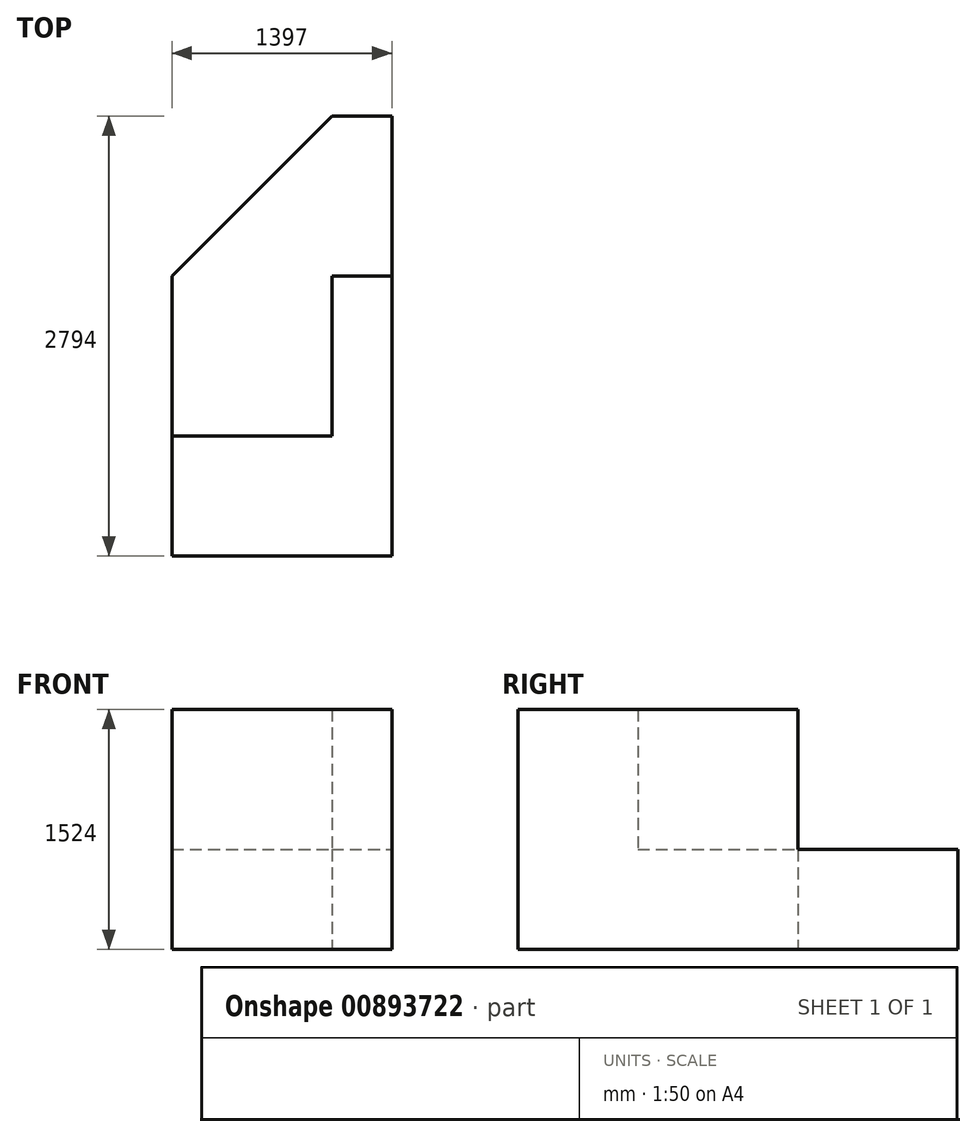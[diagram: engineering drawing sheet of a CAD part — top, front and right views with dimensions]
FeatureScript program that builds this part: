
annotation { "Feature Type Name" : "Feature", "Feature Type Description" : "" }
export const myFeature = defineFeature(function(context is Context, id is Id, definition is map)
    precondition{}
    {
        {
            var Q0;
            Q0=qCreatedBy(makeId("Top.planeOp"),FACE);
            var sketch = newSketch(context, id + "F0", { "sketchPlane" : qUnion([Q0])});
            skLineSegment(sketch, "E0", {"start": v(0, 0) * mm, "end": v(1397, 0) * mm});
            skLineSegment(sketch, "E1", {"start": v(1397, 0) * mm, "end": v(1397, 2794) * mm});
            skLineSegment(sketch, "E2", {"start": v(1397, 2794) * mm, "end": v(1016, 2794) * mm});
            skLineSegment(sketch, "E3", {"start": v(0, 0) * mm, "end": v(0, 1778) * mm});
            skLineSegment(sketch, "E4", {"start": v(1016, 2794) * mm, "end": v(0, 1778) * mm});
            skSolve(sketch);
        }
        {
            var Q0;
            Q0=makeQuery(id+"F0.imprint","IMPRINT",FACE,{"disambiguationData":[TD([[makeQuery(id+"F0.imprint","IMPRINT",EDGE,{"derivedFrom":sQuery(id+"F0.wireOp",EDGE,"E0")}),1.0]])]});
            extrude(context, id + "F1", {"entities" : qUnion([Q0]), "depth" : 635 * mm, "offsetDistance" : 25.4 * mm});
        }
        {
            var Q0;
            Q0=makeQuery(id+"F1.opExtrude","CAP_FACE",FACE,{"disambiguationData":[OSD([sQuery(id+"F0.wireOp",EDGE,"E0"),sQuery(id+"F0.wireOp",EDGE,"E1"),sQuery(id+"F0.wireOp",EDGE,"E2"),sQuery(id+"F0.wireOp",EDGE,"E3"),sQuery(id+"F0.wireOp",EDGE,"E4")])],"isStart":false});
            var sketch = newSketch(context, id + "F2", { "sketchPlane" : qUnion([Q0])});
            skLineSegment(sketch, "E5", {"start": v(0, 0) * mm, "end": v(0, 762) * mm});
            skLineSegment(sketch, "E6", {"start": v(0, 762) * mm, "end": v(1016, 762) * mm});
            skLineSegment(sketch, "E7", {"start": v(1016, 762) * mm, "end": v(1016, 0) * mm});
            skLineSegment(sketch, "E8", {"start": v(1016, 0) * mm, "end": v(0, 0) * mm});
            skSolve(sketch);
        }
        {
            var Q0;
            Q0=makeQuery(id+"F2.imprint","IMPRINT",FACE,{"disambiguationData":[TD([[makeQuery(id+"F2.imprint","IMPRINT",EDGE,{"derivedFrom":sQuery(id+"F2.wireOp",EDGE,"E5")}),-1.0]])]});
            extrude(context, id + "F3", {"entities" : qUnion([Q0]), "operationType" : NewBodyOperationType.ADD, "depth" : 889 * mm, "offsetDistance" : 25.4 * mm});
        }
        {
            var Q0;
            Q0=makeQuery(id+"F1.opExtrude","CAP_FACE",FACE,{"disambiguationData":[OSD([sQuery(id+"F0.wireOp",EDGE,"E0"),sQuery(id+"F0.wireOp",EDGE,"E1"),sQuery(id+"F0.wireOp",EDGE,"E2"),sQuery(id+"F0.wireOp",EDGE,"E3"),sQuery(id+"F0.wireOp",EDGE,"E4")])],"isStart":false});
            var sketch = newSketch(context, id + "F4", { "sketchPlane" : qUnion([Q0])});
            skLineSegment(sketch, "E9", {"start": v(1016, 0) * mm, "end": v(1016, 1778) * mm});
            skLineSegment(sketch, "E10", {"start": v(1016, 1778) * mm, "end": v(1397, 1778) * mm});
            skLineSegment(sketch, "E11", {"start": v(1397, 1778) * mm, "end": v(1397, 0) * mm});
            skLineSegment(sketch, "E12", {"start": v(1397, 0) * mm, "end": v(1016, 0) * mm});
            skSolve(sketch);
        }
        {
            var Q0;
            {var subQ0=sQuery(id+"F4.wireOp",EDGE,"E10");Q0=makeQuery(id+"F4.imprint","IMPRINT",FACE,{"disambiguationData":[TD([[makeQuery(id+"F4.imprint","IMPRINT",EDGE,{"derivedFrom":subQ0}),-1.0]])]});}
            extrude(context, id + "F5", {"entities" : qUnion([Q0]), "operationType" : NewBodyOperationType.ADD, "depth" : 889 * mm, "offsetDistance" : 25.4 * mm});
        }
    });
